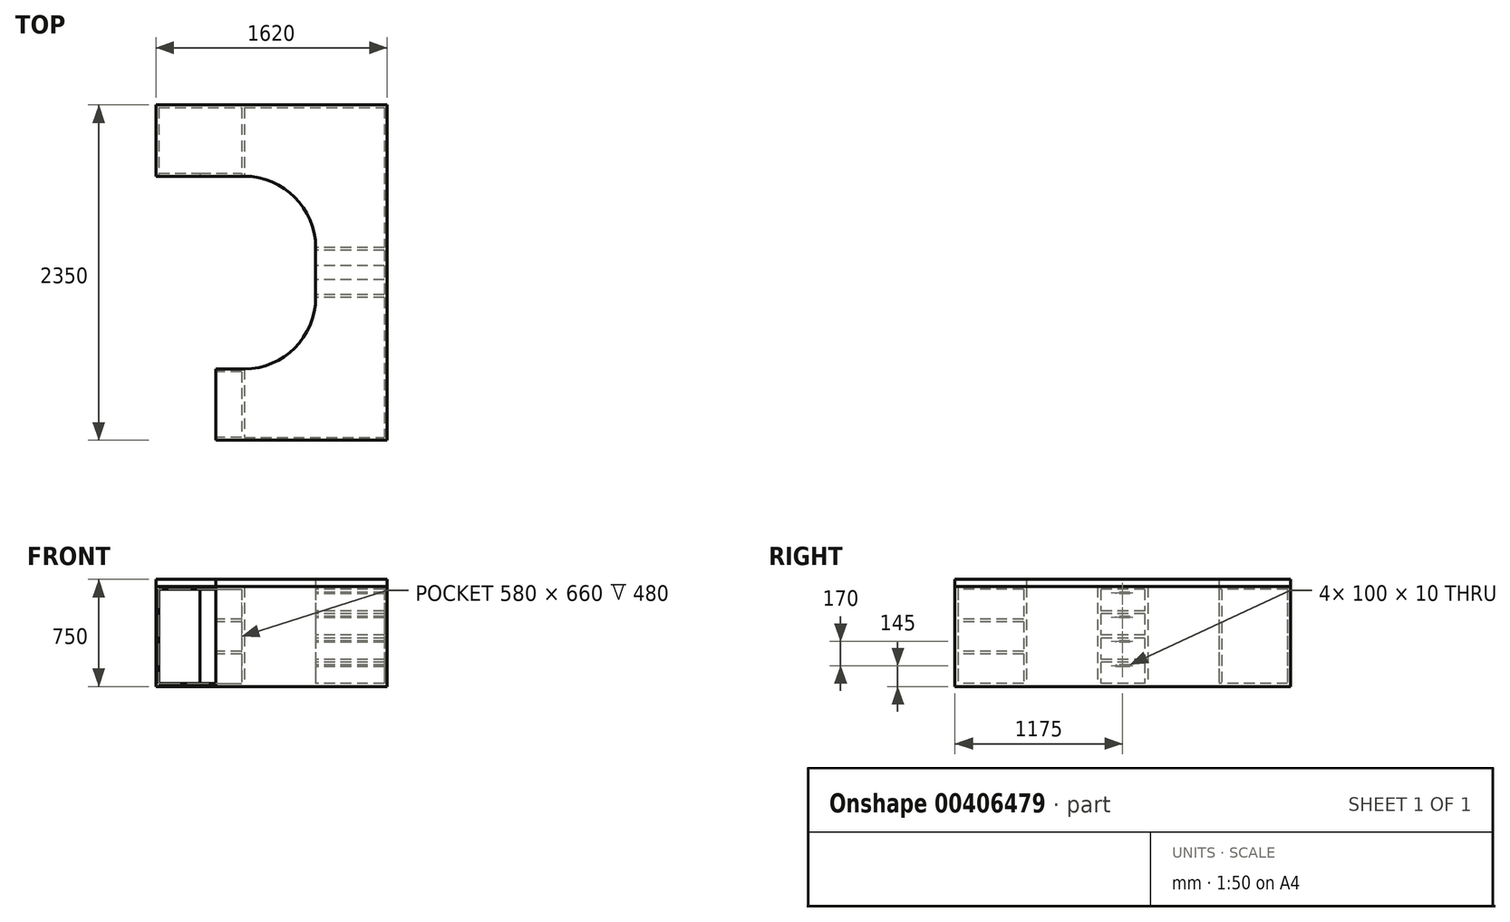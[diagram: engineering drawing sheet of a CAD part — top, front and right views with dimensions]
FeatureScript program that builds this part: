
annotation { "Feature Type Name" : "Feature", "Feature Type Description" : "" }
export const myFeature = defineFeature(function(context is Context, id is Id, definition is map)
    precondition{}
    {
        {
            var Q0;
            Q0=qCreatedBy(makeId("Top.planeOp"),FACE);
            var sketch = newSketch(context, id + "F0", { "sketchPlane" : qUnion([Q0])});
            skLineSegment(sketch, "E0", {"start": v(0, 1175) * mm, "end": v(620, 1175) * mm});
            skLineSegment(sketch, "E1", {"start": v(620, 1175) * mm, "end": v(1620, 1175) * mm});
            skLineSegment(sketch, "E2", {"start": v(1620, 1175) * mm, "end": v(1620, 175) * mm});
            skLineSegment(sketch, "E3", {"start": v(1620, 175) * mm, "end": v(1620, -175) * mm});
            skLineSegment(sketch, "E4", {"start": v(1620, -175) * mm, "end": v(1620, -1175) * mm});
            skLineSegment(sketch, "E5", {"start": v(1620, -1175) * mm, "end": v(620, -1175) * mm});
            skLineSegment(sketch, "E6", {"start": v(620, -1175) * mm, "end": v(0, -1175) * mm});
            skLineSegment(sketch, "E7", {"start": v(0, -1175) * mm, "end": v(0, -675) * mm});
            skLineSegment(sketch, "E8", {"start": v(0, -675) * mm, "end": v(620, -675) * mm});
            skLineSegment(sketch, "E9", {"start": v(1120, -175) * mm, "end": v(1120, 175) * mm});
            skLineSegment(sketch, "E10", {"start": v(620, 675) * mm, "end": v(0, 675) * mm});
            skLineSegment(sketch, "E11", {"start": v(0, 675) * mm, "end": v(0, 1175) * mm});
            skLineSegment(sketch, "E12", {"start": v(-331.74, 0) * mm, "end": v(331.74, 0) * mm, "construction": true});
            skLineSegment(sketch, "E13", {"start": v(620, 1175) * mm, "end": v(620, -1175) * mm, "construction": true});
            skLineSegment(sketch, "E14", {"start": v(1620, -175) * mm, "end": v(620, -175) * mm, "construction": true});
            skLineSegment(sketch, "E15", {"start": v(1620, 175) * mm, "end": v(620, 175) * mm, "construction": true});
            skArc(sketch, "E16.filletArc", {"start": v(620, -675) * mm, "mid": v(973.55, -528.55) * mm, "end": v(1120, -175) * mm});
            skArc(sketch, "E17.filletArc", {"start": v(1120, 175) * mm, "mid": v(973.55, 528.55) * mm, "end": v(620, 675) * mm});
            skLineSegment(sketch, "E18", {"start": v(1620, 175) * mm, "end": v(1120, 175) * mm});
            skLineSegment(sketch, "E19", {"start": v(1620, -175) * mm, "end": v(1120, -175) * mm});
            skLineSegment(sketch, "E20", {"start": v(620, 1175) * mm, "end": v(620, 675) * mm});
            skLineSegment(sketch, "E21", {"start": v(620, -675) * mm, "end": v(620, -1175) * mm});
            skLineSegment(sketch, "E22", {"start": v(620, 1155) * mm, "end": v(1620, 1155) * mm});
            skLineSegment(sketch, "E23", {"start": v(620, -1155) * mm, "end": v(1620, -1155) * mm});
            skLineSegment(sketch, "E24", {"start": v(1600, 1155) * mm, "end": v(1600, -1155) * mm});
            skLineSegment(sketch, "E25", {"start": v(420, -675) * mm, "end": v(420, -1175) * mm});
            skSolve(sketch);
        }
        {
            var Q0;
            {var subQ1=sQuery(id+"F0.wireOp",EDGE,"E5");Q0=makeQuery(id+"F0.imprint","IMPRINT",FACE,{"disambiguationData":[TD([[makeQuery(id+"F0.imprint","IMPRINT",EDGE,{"derivedFrom":subQ1}),-1.0]])]});}
            var Q1;
            {var subQ1=sQuery(id+"F0.wireOp",EDGE,"E4");var subQ3=sQuery(id+"F0.wireOp",EDGE,"E23");var subQ4=makeQuery(id+"F0.imprint","INTERSECT",VERTEX,{"derivedFrom":[subQ1,subQ3]});Q1=makeQuery(id+"F0.imprint","IMPRINT",FACE,{"disambiguationData":[TD([[makeQuery(id+"F0.imprint","IMPRINT",EDGE,{"disambiguationData":[TD([[subQ4,1.0]])],"derivedFrom":subQ3}),1.0]])]});}
            var Q2;
            {var subQ0=sQuery(id+"F0.wireOp",EDGE,"E9");Q2=makeQuery(id+"F0.imprint","IMPRINT",FACE,{"disambiguationData":[TD([[makeQuery(id+"F0.imprint","IMPRINT",EDGE,{"derivedFrom":subQ0}),-1.0]])]});}
            var Q3;
            {var subQ0=sQuery(id+"F0.wireOp",EDGE,"E3");Q3=makeQuery(id+"F0.imprint","IMPRINT",FACE,{"disambiguationData":[TD([[makeQuery(id+"F0.imprint","IMPRINT",EDGE,{"derivedFrom":subQ0}),-1.0]])]});}
            var Q4;
            {var subQ1=sQuery(id+"F0.wireOp",EDGE,"E2");var subQ3=sQuery(id+"F0.wireOp",EDGE,"E22");var subQ4=makeQuery(id+"F0.imprint","INTERSECT",VERTEX,{"derivedFrom":[subQ1,subQ3]});Q4=makeQuery(id+"F0.imprint","IMPRINT",FACE,{"disambiguationData":[TD([[makeQuery(id+"F0.imprint","IMPRINT",EDGE,{"disambiguationData":[TD([[subQ4,1.0]])],"derivedFrom":subQ3}),-1.0]])]});}
            var Q5;
            {var subQ2=sQuery(id+"F0.wireOp",EDGE,"E0");Q5=makeQuery(id+"F0.imprint","IMPRINT",FACE,{"disambiguationData":[TD([[makeQuery(id+"F0.imprint","IMPRINT",EDGE,{"derivedFrom":subQ2}),-1.0]])]});}
            var Q6;
            {var subQ5=sQuery(id+"F0.wireOp",EDGE,"E1");Q6=makeQuery(id+"F0.imprint","IMPRINT",FACE,{"disambiguationData":[TD([[makeQuery(id+"F0.imprint","IMPRINT",EDGE,{"derivedFrom":subQ5}),-1.0]])]});}
            var Q7;
            {var subQ6=sQuery(id+"F0.wireOp",EDGE,"E25");Q7=makeQuery(id+"F0.imprint","IMPRINT",FACE,{"disambiguationData":[TD([[makeQuery(id+"F0.imprint","IMPRINT",EDGE,{"derivedFrom":subQ6}),1.0]])]});}
            extrude(context, id + "F1", {"entities" : qUnion([Q0, Q1, Q2, Q3, Q4, Q5, Q6, Q7]), "depth" : 700 * mm, "offsetDistance" : 25 * mm});
        }
        {
            var Q0;
            {var subQ2=sQuery(id+"F0.wireOp",EDGE,"E0");Q0=makeQuery(id+"F0.imprint","IMPRINT",FACE,{"disambiguationData":[TD([[makeQuery(id+"F0.imprint","IMPRINT",EDGE,{"derivedFrom":subQ2}),-1.0]])]});}
            var Q1;
            {var subQ5=sQuery(id+"F0.wireOp",EDGE,"E1");Q1=makeQuery(id+"F0.imprint","IMPRINT",FACE,{"disambiguationData":[TD([[makeQuery(id+"F0.imprint","IMPRINT",EDGE,{"derivedFrom":subQ5}),-1.0]])]});}
            var Q2;
            {var subQ5=sQuery(id+"F0.wireOp",EDGE,"E17.filletArc");Q2=makeQuery(id+"F0.imprint","IMPRINT",FACE,{"disambiguationData":[TD([[makeQuery(id+"F0.imprint","IMPRINT",EDGE,{"derivedFrom":subQ5}),-1.0]])]});}
            var Q3;
            {var subQ1=sQuery(id+"F0.wireOp",EDGE,"E2");var subQ3=sQuery(id+"F0.wireOp",EDGE,"E22");var subQ4=makeQuery(id+"F0.imprint","INTERSECT",VERTEX,{"derivedFrom":[subQ1,subQ3]});Q3=makeQuery(id+"F0.imprint","IMPRINT",FACE,{"disambiguationData":[TD([[makeQuery(id+"F0.imprint","IMPRINT",EDGE,{"disambiguationData":[TD([[subQ4,1.0]])],"derivedFrom":subQ3}),-1.0]])]});}
            var Q4;
            {var subQ0=sQuery(id+"F0.wireOp",EDGE,"E3");Q4=makeQuery(id+"F0.imprint","IMPRINT",FACE,{"disambiguationData":[TD([[makeQuery(id+"F0.imprint","IMPRINT",EDGE,{"derivedFrom":subQ0}),-1.0]])]});}
            var Q5;
            {var subQ0=sQuery(id+"F0.wireOp",EDGE,"E9");Q5=makeQuery(id+"F0.imprint","IMPRINT",FACE,{"disambiguationData":[TD([[makeQuery(id+"F0.imprint","IMPRINT",EDGE,{"derivedFrom":subQ0}),-1.0]])]});}
            var Q6;
            {var subQ1=sQuery(id+"F0.wireOp",EDGE,"E4");var subQ3=sQuery(id+"F0.wireOp",EDGE,"E23");var subQ4=makeQuery(id+"F0.imprint","INTERSECT",VERTEX,{"derivedFrom":[subQ1,subQ3]});Q6=makeQuery(id+"F0.imprint","IMPRINT",FACE,{"disambiguationData":[TD([[makeQuery(id+"F0.imprint","IMPRINT",EDGE,{"disambiguationData":[TD([[subQ4,1.0]])],"derivedFrom":subQ3}),1.0]])]});}
            var Q7;
            {var subQ1=sQuery(id+"F0.wireOp",EDGE,"E5");Q7=makeQuery(id+"F0.imprint","IMPRINT",FACE,{"disambiguationData":[TD([[makeQuery(id+"F0.imprint","IMPRINT",EDGE,{"derivedFrom":subQ1}),-1.0]])]});}
            var Q8;
            {var subQ5=sQuery(id+"F0.wireOp",EDGE,"E16.filletArc");Q8=makeQuery(id+"F0.imprint","IMPRINT",FACE,{"disambiguationData":[TD([[makeQuery(id+"F0.imprint","IMPRINT",EDGE,{"derivedFrom":subQ5}),-1.0]])]});}
            var Q9;
            {var subQ6=sQuery(id+"F0.wireOp",EDGE,"E25");Q9=makeQuery(id+"F0.imprint","IMPRINT",FACE,{"disambiguationData":[TD([[makeQuery(id+"F0.imprint","IMPRINT",EDGE,{"derivedFrom":subQ6}),1.0]])]});}
            extrude(context, id + "F2", {"entities" : qUnion([Q0, Q1, Q2, Q3, Q4, Q5, Q6, Q7, Q8, Q9]), "depth" : 750 * mm, "offsetDistance" : 25 * mm, "hasSecondDirection" : true, "secondDirectionOppositeDirection" : false, "secondDirectionDepth" : 700 * mm});
        }
        {
            var Q0;
            Q0=makeQuery(id+"F1.opExtrude","SWEPT_FACE",FACE,{"disambiguationData":[OSD([sQuery(id+"F0.wireOp",EDGE,"E9")])]});
            var sketch = newSketch(context, id + "F3", { "sketchPlane" : qUnion([Q0])});
            skLineSegment(sketch, "E26.bottom", {"start": v(-155, 680) * mm, "end": v(155, 680) * mm});
            skLineSegment(sketch, "E26.top", {"start": v(-155, 530) * mm, "end": v(155, 530) * mm});
            skLineSegment(sketch, "E26.left", {"start": v(-155, 680) * mm, "end": v(-155, 530) * mm});
            skLineSegment(sketch, "E26.right", {"start": v(155, 680) * mm, "end": v(155, 530) * mm});
            skLineSegment(sketch, "E27.bottom", {"start": v(-155, 510) * mm, "end": v(155, 510) * mm});
            skLineSegment(sketch, "E27.top", {"start": v(-155, 360) * mm, "end": v(155, 360) * mm});
            skLineSegment(sketch, "E27.left", {"start": v(-155, 510) * mm, "end": v(-155, 360) * mm});
            skLineSegment(sketch, "E27.right", {"start": v(155, 510) * mm, "end": v(155, 360) * mm});
            skLineSegment(sketch, "E28.bottom", {"start": v(-155, 340) * mm, "end": v(155, 340) * mm});
            skLineSegment(sketch, "E28.top", {"start": v(-155, 190) * mm, "end": v(155, 190) * mm});
            skLineSegment(sketch, "E28.left", {"start": v(-155, 340) * mm, "end": v(-155, 190) * mm});
            skLineSegment(sketch, "E28.right", {"start": v(155, 340) * mm, "end": v(155, 190) * mm});
            skLineSegment(sketch, "E29.bottom", {"start": v(-155, 170) * mm, "end": v(155, 170) * mm});
            skLineSegment(sketch, "E29.top", {"start": v(-155, 20) * mm, "end": v(155, 20) * mm});
            skLineSegment(sketch, "E29.left", {"start": v(-155, 170) * mm, "end": v(-155, 20) * mm});
            skLineSegment(sketch, "E29.right", {"start": v(155, 170) * mm, "end": v(155, 20) * mm});
            skSolve(sketch);
        }
        {
            var Q0;
            Q0=makeQuery(id+"F3.imprint","IMPRINT",FACE,{"disambiguationData":[TD([[makeQuery(id+"F3.imprint","IMPRINT",EDGE,{"derivedFrom":sQuery(id+"F3.wireOp",EDGE,"E26.bottom")}),-1.0]])]});
            var Q1;
            Q1=makeQuery(id+"F3.imprint","IMPRINT",FACE,{"disambiguationData":[TD([[makeQuery(id+"F3.imprint","IMPRINT",EDGE,{"derivedFrom":sQuery(id+"F3.wireOp",EDGE,"E27.bottom")}),-1.0]])]});
            var Q2;
            Q2=makeQuery(id+"F3.imprint","IMPRINT",FACE,{"disambiguationData":[TD([[makeQuery(id+"F3.imprint","IMPRINT",EDGE,{"derivedFrom":sQuery(id+"F3.wireOp",EDGE,"E28.bottom")}),-1.0]])]});
            var Q3;
            Q3=makeQuery(id+"F3.imprint","IMPRINT",FACE,{"disambiguationData":[TD([[makeQuery(id+"F3.imprint","IMPRINT",EDGE,{"derivedFrom":sQuery(id+"F3.wireOp",EDGE,"E29.bottom")}),-1.0]])]});
            extrude(context, id + "F4", {"entities" : qUnion([Q0, Q1, Q2, Q3]), "operationType" : NewBodyOperationType.REMOVE, "endBound" : BoundingType.UP_TO_NEXT, "oppositeDirection" : true, "depth" : 25 * mm, "hasOffset" : true, "offsetDistance" : 20 * mm});
        }
        {
            var Q0;
            Q0=makeQuery(id+"F1.opExtrude","SWEPT_FACE",FACE,{"disambiguationData":[OSD([sQuery(id+"F0.wireOp",EDGE,"E10")])]});
            var sketch = newSketch(context, id + "F5", { "sketchPlane" : qUnion([Q0])});
            skLineSegment(sketch, "E30.bottom", {"start": v(20, 680) * mm, "end": v(600, 680) * mm});
            skLineSegment(sketch, "E30.top", {"start": v(20, 20) * mm, "end": v(600, 20) * mm});
            skLineSegment(sketch, "E30.left", {"start": v(20, 680) * mm, "end": v(20, 20) * mm});
            skLineSegment(sketch, "E30.right", {"start": v(600, 680) * mm, "end": v(600, 20) * mm});
            skLineSegment(sketch, "E31", {"start": v(310, 680) * mm, "end": v(310, 20) * mm});
            skSolve(sketch);
        }
        {
            var Q0;
            {var subQ0=sQuery(id+"F5.wireOp",EDGE,"E30.left");Q0=makeQuery(id+"F5.imprint","IMPRINT",FACE,{"disambiguationData":[TD([[makeQuery(id+"F5.imprint","IMPRINT",EDGE,{"derivedFrom":subQ0}),1.0]])]});}
            var Q1;
            {var subQ0=sQuery(id+"F5.wireOp",EDGE,"E30.right");Q1=makeQuery(id+"F5.imprint","IMPRINT",FACE,{"disambiguationData":[TD([[makeQuery(id+"F5.imprint","IMPRINT",EDGE,{"derivedFrom":subQ0}),-1.0]])]});}
            extrude(context, id + "F6", {"entities" : qUnion([Q0, Q1]), "operationType" : NewBodyOperationType.REMOVE, "endBound" : BoundingType.UP_TO_NEXT, "oppositeDirection" : true, "depth" : 25 * mm, "hasOffset" : true, "offsetDistance" : 20 * mm});
        }
        {
            var Q0;
            Q0=makeQuery(id+"F1.opExtrude","SWEPT_FACE",FACE,{"disambiguationData":[OSD([sQuery(id+"F0.wireOp",EDGE,"E25")])]});
            var sketch = newSketch(context, id + "F7", { "sketchPlane" : qUnion([Q0])});
            skLineSegment(sketch, "E32.bottom", {"start": v(695, 680) * mm, "end": v(1155, 680) * mm});
            skLineSegment(sketch, "E32.top", {"start": v(695, 473.33) * mm, "end": v(1155, 473.33) * mm});
            skLineSegment(sketch, "E32.left", {"start": v(695, 680) * mm, "end": v(695, 473.33) * mm});
            skLineSegment(sketch, "E32.right", {"start": v(1155, 680) * mm, "end": v(1155, 473.33) * mm});
            skLineSegment(sketch, "E33.bottom", {"start": v(695, 453.33) * mm, "end": v(1155, 453.33) * mm});
            skLineSegment(sketch, "E33.top", {"start": v(695, 246.67) * mm, "end": v(1155, 246.67) * mm});
            skLineSegment(sketch, "E33.left", {"start": v(695, 453.33) * mm, "end": v(695, 246.67) * mm});
            skLineSegment(sketch, "E33.right", {"start": v(1155, 453.33) * mm, "end": v(1155, 246.67) * mm});
            skLineSegment(sketch, "E34.bottom", {"start": v(695, 226.67) * mm, "end": v(1155, 226.67) * mm});
            skLineSegment(sketch, "E34.top", {"start": v(695, 20) * mm, "end": v(1155, 20) * mm});
            skLineSegment(sketch, "E34.left", {"start": v(695, 226.67) * mm, "end": v(695, 20) * mm});
            skLineSegment(sketch, "E34.right", {"start": v(1155, 226.67) * mm, "end": v(1155, 20) * mm});
            skLineSegment(sketch, "E35", {"start": v(695, 463.33) * mm, "end": v(1155, 463.33) * mm, "construction": true});
            skLineSegment(sketch, "E36", {"start": v(695, 236.67) * mm, "end": v(1155, 236.67) * mm, "construction": true});
            skSolve(sketch);
        }
        {
            var Q0;
            Q0=makeQuery(id+"F7.imprint","IMPRINT",FACE,{"disambiguationData":[TD([[makeQuery(id+"F7.imprint","IMPRINT",EDGE,{"derivedFrom":sQuery(id+"F7.wireOp",EDGE,"E32.bottom")}),-1.0]])]});
            var Q1;
            Q1=makeQuery(id+"F7.imprint","IMPRINT",FACE,{"disambiguationData":[TD([[makeQuery(id+"F7.imprint","IMPRINT",EDGE,{"derivedFrom":sQuery(id+"F7.wireOp",EDGE,"E33.bottom")}),-1.0]])]});
            var Q2;
            Q2=makeQuery(id+"F7.imprint","IMPRINT",FACE,{"disambiguationData":[TD([[makeQuery(id+"F7.imprint","IMPRINT",EDGE,{"derivedFrom":sQuery(id+"F7.wireOp",EDGE,"E34.bottom")}),-1.0]])]});
            extrude(context, id + "F8", {"entities" : qUnion([Q0, Q1, Q2]), "operationType" : NewBodyOperationType.REMOVE, "endBound" : BoundingType.UP_TO_NEXT, "oppositeDirection" : true, "depth" : 25 * mm, "hasOffset" : true, "offsetDistance" : 20 * mm});
        }
        {
            var Q0;
            Q0=makeQuery(id+"F3.imprint","IMPRINT",FACE,{"disambiguationData":[TD([[makeQuery(id+"F3.imprint","IMPRINT",EDGE,{"derivedFrom":sQuery(id+"F3.wireOp",EDGE,"E26.bottom")}),-1.0]])]});
            var Q1;
            Q1=makeQuery(id+"F3.imprint","IMPRINT",FACE,{"disambiguationData":[TD([[makeQuery(id+"F3.imprint","IMPRINT",EDGE,{"derivedFrom":sQuery(id+"F3.wireOp",EDGE,"E27.bottom")}),-1.0]])]});
            var Q2;
            Q2=makeQuery(id+"F3.imprint","IMPRINT",FACE,{"disambiguationData":[TD([[makeQuery(id+"F3.imprint","IMPRINT",EDGE,{"derivedFrom":sQuery(id+"F3.wireOp",EDGE,"E28.bottom")}),-1.0]])]});
            var Q3;
            Q3=makeQuery(id+"F3.imprint","IMPRINT",FACE,{"disambiguationData":[TD([[makeQuery(id+"F3.imprint","IMPRINT",EDGE,{"derivedFrom":sQuery(id+"F3.wireOp",EDGE,"E29.bottom")}),-1.0]])]});
            extrude(context, id + "F9", {"entities" : qUnion([Q0, Q1, Q2, Q3]), "endBound" : BoundingType.UP_TO_NEXT, "oppositeDirection" : true, "depth" : 25 * mm, "offsetDistance" : 25 * mm});
        }
        {
            var Q0;
            {var subQ0=sQuery(id+"F5.wireOp",EDGE,"E30.left");Q0=makeQuery(id+"F5.imprint","IMPRINT",FACE,{"disambiguationData":[TD([[makeQuery(id+"F5.imprint","IMPRINT",EDGE,{"derivedFrom":subQ0}),1.0]])]});}
            extrude(context, id + "F10", {"entities" : qUnion([Q0]), "oppositeDirection" : true, "depth" : 20 * mm, "offsetDistance" : 25 * mm});
        }
        {
            var Q0;
            {var subQ0=sQuery(id+"F5.wireOp",EDGE,"E30.right");Q0=makeQuery(id+"F5.imprint","IMPRINT",FACE,{"disambiguationData":[TD([[makeQuery(id+"F5.imprint","IMPRINT",EDGE,{"derivedFrom":subQ0}),-1.0]])]});}
            extrude(context, id + "F11", {"entities" : qUnion([Q0]), "oppositeDirection" : true, "depth" : 20 * mm, "offsetDistance" : 25 * mm});
        }
        {
            var Q0;
            Q0=makeQuery(id+"F9.opExtrude","CAP_FACE",FACE,{"disambiguationData":[OSD([sQuery(id+"F3.wireOp",EDGE,"E26.bottom"),sQuery(id+"F3.wireOp",EDGE,"E26.top"),sQuery(id+"F3.wireOp",EDGE,"E26.left"),sQuery(id+"F3.wireOp",EDGE,"E26.right")])],"isStart":true});
            var sketch = newSketch(context, id + "F12", { "sketchPlane" : qUnion([Q0])});
            skLineSegment(sketch, "E37.bottom", {"start": v(-50, 660) * mm, "end": v(50, 660) * mm});
            skLineSegment(sketch, "E37.top", {"start": v(-50, 650) * mm, "end": v(50, 650) * mm});
            skLineSegment(sketch, "E37.left", {"start": v(-50, 660) * mm, "end": v(-50, 650) * mm});
            skLineSegment(sketch, "E37.right", {"start": v(50, 660) * mm, "end": v(50, 650) * mm});
            skLineSegment(sketch, "E38.bottom", {"start": v(-50, 490) * mm, "end": v(50, 490) * mm});
            skLineSegment(sketch, "E38.top", {"start": v(-50, 480) * mm, "end": v(50, 480) * mm});
            skLineSegment(sketch, "E38.left", {"start": v(-50, 490) * mm, "end": v(-50, 480) * mm});
            skLineSegment(sketch, "E38.right", {"start": v(50, 490) * mm, "end": v(50, 480) * mm});
            skLineSegment(sketch, "E39.bottom", {"start": v(-50, 320) * mm, "end": v(50, 320) * mm});
            skLineSegment(sketch, "E39.top", {"start": v(-50, 310) * mm, "end": v(50, 310) * mm});
            skLineSegment(sketch, "E39.left", {"start": v(-50, 320) * mm, "end": v(-50, 310) * mm});
            skLineSegment(sketch, "E39.right", {"start": v(50, 320) * mm, "end": v(50, 310) * mm});
            skLineSegment(sketch, "E40.bottom", {"start": v(-50, 150) * mm, "end": v(50, 150) * mm});
            skLineSegment(sketch, "E40.top", {"start": v(-50, 140) * mm, "end": v(50, 140) * mm});
            skLineSegment(sketch, "E40.left", {"start": v(-50, 150) * mm, "end": v(-50, 140) * mm});
            skLineSegment(sketch, "E40.right", {"start": v(50, 150) * mm, "end": v(50, 140) * mm});
            skLineSegment(sketch, "E41", {"start": v(0, 680) * mm, "end": v(0, 530) * mm, "construction": true});
            skSolve(sketch);
        }
        {
            var Q0;
            Q0 = qSketchRegion(id + "F12", true);
            extrude(context, id + "F13", {"entities" : qUnion([Q0]), "operationType" : NewBodyOperationType.REMOVE, "endBound" : BoundingType.UP_TO_NEXT, "oppositeDirection" : true, "depth" : 25 * mm, "offsetDistance" : 25 * mm});
        }
    });
